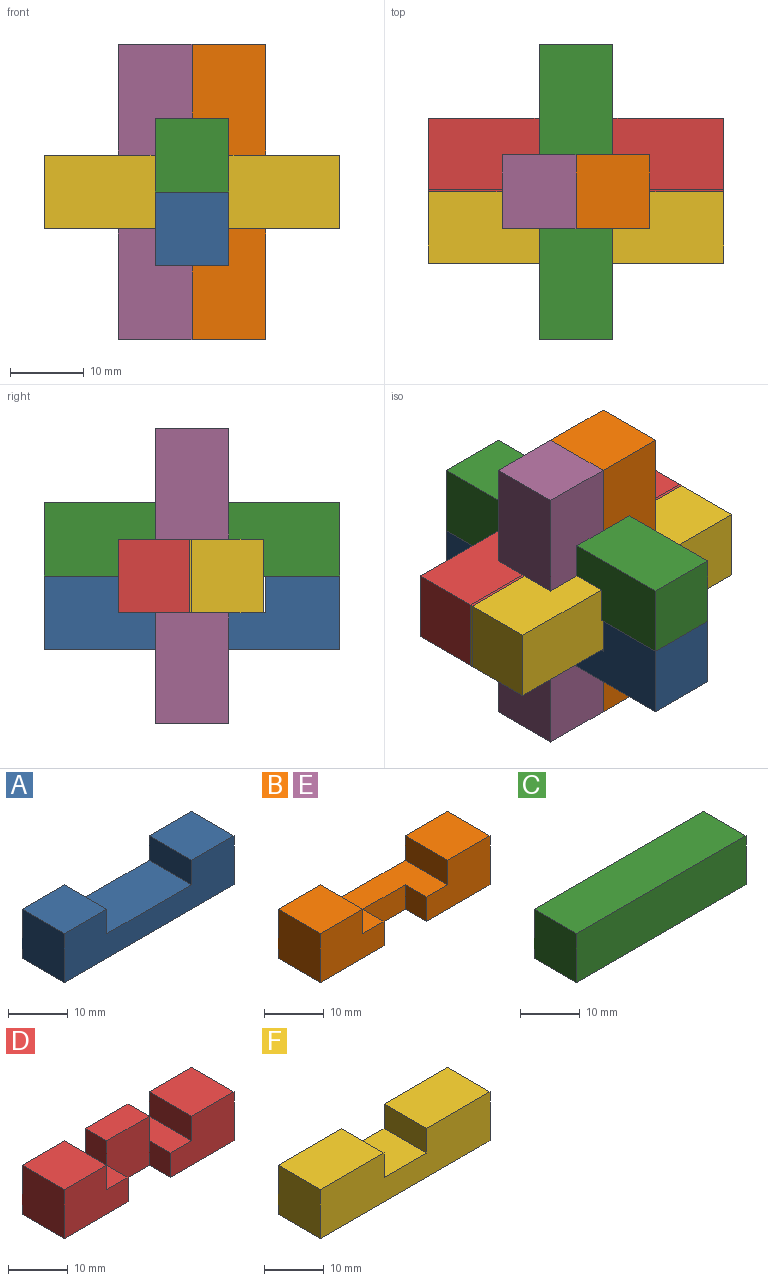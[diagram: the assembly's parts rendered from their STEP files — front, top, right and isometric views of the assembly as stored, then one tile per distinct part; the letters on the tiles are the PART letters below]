
ASSEMBLY  parts=6 mates=5
PART A: 10 faces, bbox 40x10x10 mm
  f0: plane 40x10mm, normal (0,-1,0), area 300mm2, adj f1,f3,f4,f5,f6,f7,f8,f9
  f1: plane 10x10mm, normal (0,0,1), area 100mm2, adj f0,f2,f4,f9
  f2: plane 40x10mm, normal (0,1,0), area 300mm2, adj f1,f3,f4,f5,f6,f7,f8,f9
  f3: plane 10x10mm, normal (-1,0,0), area 100mm2, adj f0,f2,f5,f6
  f4: plane 10x10mm, normal (1,0,0), area 100mm2, adj f0,f1,f2,f6
  f5: plane 10x10mm, normal (0,0,1), area 100mm2, adj f0,f2,f3,f7
  f6: plane 40x10mm, normal (0,0,-1), area 400mm2, adj f0,f2,f3,f4
  f7: plane 10x5mm, normal (1,0,0), area 50mm2, adj f0,f2,f5,f8
  f8: plane 20x10mm, normal (0,0,1), area 200mm2, adj f0,f2,f7,f9
  f9: plane 10x5mm, normal (-1,0,0), area 50mm2, adj f0,f1,f2,f8
PART B: 14 faces, bbox 40x10x10 mm
  f0: plane 15x10mm, normal (0,-1,0), area 125mm2, adj f1,f3,f6,f9,f10,f11
  f1: plane 40x10mm, normal (0,0,-1), area 350mm2, adj f0,f2,f4,f5,f6,f11,f12,f13
  f2: plane 15x10mm, normal (0,-1,0), area 125mm2, adj f1,f5,f7,f8,f9,f12
  f3: plane 10x10mm, normal (0,0,1), area 100mm2, adj f0,f4,f6,f10
  f4: plane 40x10mm, normal (0,1,0), area 300mm2, adj f1,f3,f5,f6,f7,f8,f9,f10
  f5: plane 10x10mm, normal (-1,0,0), area 100mm2, adj f1,f2,f4,f7
  f6: plane 10x10mm, normal (1,0,0), area 100mm2, adj f0,f1,f3,f4
  f7: plane 10x10mm, normal (0,0,1), area 100mm2, adj f2,f4,f5,f8
  f8: plane 10x5mm, normal (1,0,0), area 50mm2, adj f2,f4,f7,f9
  f9: plane 20x10mm, normal (0,0,1), area 150mm2, adj f0,f2,f4,f8,f10,f11,f12,f13
  f10: plane 10x5mm, normal (-1,0,0), area 50mm2, adj f0,f3,f4,f9
  f11: plane 5x5mm, normal (-1,0,0), area 25mm2, adj f0,f1,f9,f13
  f12: plane 5x5mm, normal (1,0,0), area 25mm2, adj f1,f2,f9,f13
  f13: plane 10x5mm, normal (0,-1,0), area 50mm2, adj f1,f9,f11,f12
PART C: 6 faces, bbox 40x10x10 mm
  f0: plane 40x10mm, normal (0,1,0), area 400mm2, adj f1,f3,f4,f5
  f1: plane 10x10mm, normal (-1,0,0), area 100mm2, adj f0,f2,f4,f5
  f2: plane 40x10mm, normal (0,-1,0), area 400mm2, adj f1,f3,f4,f5
  f3: plane 10x10mm, normal (1,0,0), area 100mm2, adj f0,f2,f4,f5
  f4: plane 40x10mm, normal (0,0,1), area 400mm2, adj f0,f1,f2,f3
  f5: plane 40x10mm, normal (0,0,-1), area 400mm2, adj f0,f1,f2,f3
PART D: 18 faces, bbox 40x10x10 mm
  f0: plane 10x5mm, normal (0,0,1), area 50mm2, adj f1,f5,f11,f12,f16
  f1: plane 15x10mm, normal (0,-1,0), area 125mm2, adj f0,f2,f4,f7,f11,f12
  f2: plane 40x10mm, normal (0,0,-1), area 350mm2, adj f1,f3,f5,f6,f7,f12,f13,f14
  f3: plane 15x10mm, normal (0,-1,0), area 125mm2, adj f2,f6,f8,f9,f10,f13
  f4: plane 10x10mm, normal (0,0,1), area 100mm2, adj f1,f5,f7,f11
  f5: plane 40x10mm, normal (0,1,0), area 350mm2, adj f0,f2,f4,f6,f7,f8,f9,f10
  f6: plane 10x10mm, normal (-1,0,0), area 100mm2, adj f2,f3,f5,f8
  f7: plane 10x10mm, normal (1,0,0), area 100mm2, adj f1,f2,f4,f5
  f8: plane 10x10mm, normal (0,0,1), area 100mm2, adj f3,f5,f6,f9
  f9: plane 10x5mm, normal (1,0,0), area 50mm2, adj f3,f5,f8,f10
  f10: plane 10x5mm, normal (0,0,1), area 50mm2, adj f3,f5,f9,f13,f15
  f11: plane 10x5mm, normal (-1,0,0), area 50mm2, adj f0,f1,f4,f5
  f12: plane 5x5mm, normal (-1,0,0), area 25mm2, adj f0,f1,f2,f14
  f13: plane 5x5mm, normal (1,0,0), area 25mm2, adj f2,f3,f10,f14
  f14: plane 10x10mm, normal (0,-1,0), area 100mm2, adj f2,f12,f13,f15,f16,f17
  f15: plane 5x5mm, normal (-1,0,0), area 25mm2, adj f5,f10,f14,f17
  f16: plane 5x5mm, normal (1,0,0), area 25mm2, adj f0,f5,f14,f17
  f17: plane 10x5mm, normal (0,0,1), area 50mm2, adj f5,f14,f15,f16
PART E: same geometry as B
PART F: 10 faces, bbox 40x10x10 mm
  f0: plane 40x10mm, normal (0,-1,0), area 350mm2, adj f1,f3,f4,f5,f6,f7,f8,f9
  f1: plane 15x10mm, normal (0,0,1), area 150mm2, adj f0,f2,f4,f9
  f2: plane 40x10mm, normal (0,1,0), area 350mm2, adj f1,f3,f4,f5,f6,f7,f8,f9
  f3: plane 10x10mm, normal (-1,0,0), area 100mm2, adj f0,f2,f5,f6
  f4: plane 10x10mm, normal (1,0,0), area 100mm2, adj f0,f1,f2,f6
  f5: plane 15x10mm, normal (0,0,1), area 150mm2, adj f0,f2,f3,f7
  f6: plane 40x10mm, normal (0,0,-1), area 400mm2, adj f0,f2,f3,f4
  f7: plane 10x5mm, normal (1,0,0), area 50mm2, adj f0,f2,f5,f8
  f8: plane 10x10mm, normal (0,0,1), area 100mm2, adj f0,f2,f7,f9
  f9: plane 10x5mm, normal (-1,0,0), area 50mm2, adj f0,f1,f2,f8
PLACE A rot(axis=(0,0,1),90deg) t=(0,5,10)mm
PLACE B rot(axis=(0,-1,0),90deg) t=(10,5,20)mm
PLACE C rot(axis=(0,0,1),90deg) t=(0,5,20)mm
PLACE D rot(axis=(0,-0.71,0.71),180deg) t=(0,15,20)mm
PLACE E rot(axis=(0,1,0),90deg) t=(-10,5,20)mm
PLACE F t=(0,0.36,15)mm
MATE slider F.f3 <-> B.f1  axis (-1,0,0) through (-20,5.36,20)mm
MATE slider A.f4 <-> E.f0  axis (0,1,0) through (0,25,10)mm
MATE fastened D.f2 <-> A.f9  axis (0,1,0) through (0,15,15)mm
MATE fastened E.f7 <-> B.f3  axis (1,0,0) through (0,5,35)mm
MATE slider C.f3 <-> B.f0  axis (0,1,0) through (0,25,30)mm
